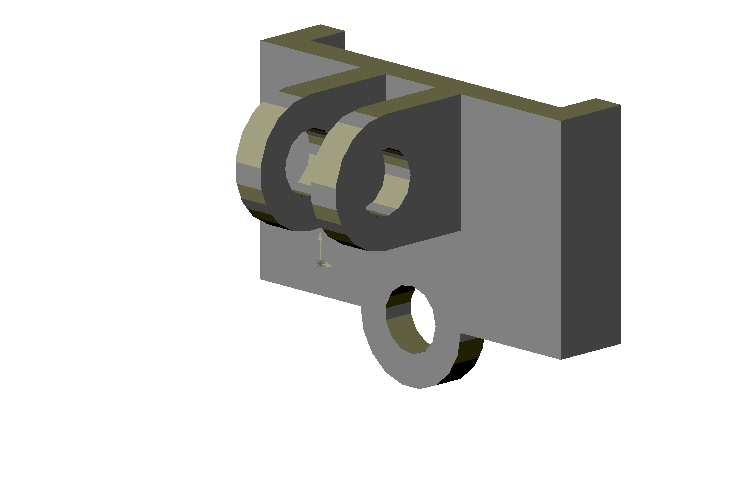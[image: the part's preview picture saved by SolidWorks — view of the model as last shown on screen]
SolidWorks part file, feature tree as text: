
SOLIDWORKS PART (.sldprt)
format: sldprt  version: not decoded by parser v0  size: 128,512 bytes
history: native  units: mm
features: sketch x7, extrude x4, plane x3, cut_extrude x3, material x1 (+9 scaffold rows collapsed)
feature tree (27):
  scaffold x9  (default folders/planes/origin — collapsed)
  material  "Material <not specified>"
  plane  "Plane1"
  plane  "Plane2"
  plane  "Plane3"
  sketch  "Sketch1"  dims[D1=28.0mm]
  extrude  "Base-Extrude"  Depth=12mm
  sketch  "Sketch2"
  cut_extrude  "Cut-Extrude1"  Depth=12mm
  sketch  "Sketch3"
  cut_extrude  "Cut-Extrude2"  Depth=60mm
  sketch  "Sketch4"
  extrude  "Boss-Extrude1"  Depth=15mm
  sketch  "Sketch5"
  extrude  "Boss-Extrude2"  Depth=5mm
  sketch  "Sketch6"
  extrude  "Boss-Extrude3"  Depth=5mm
  sketch  "Sketch7"
  cut_extrude  "Cut-Extrude3"  Depth=40mm
decode coverage: 8 of 14 modeling features carry decoded parameters
note: suppression state not decoded; provenance and decode notes live in map.json
